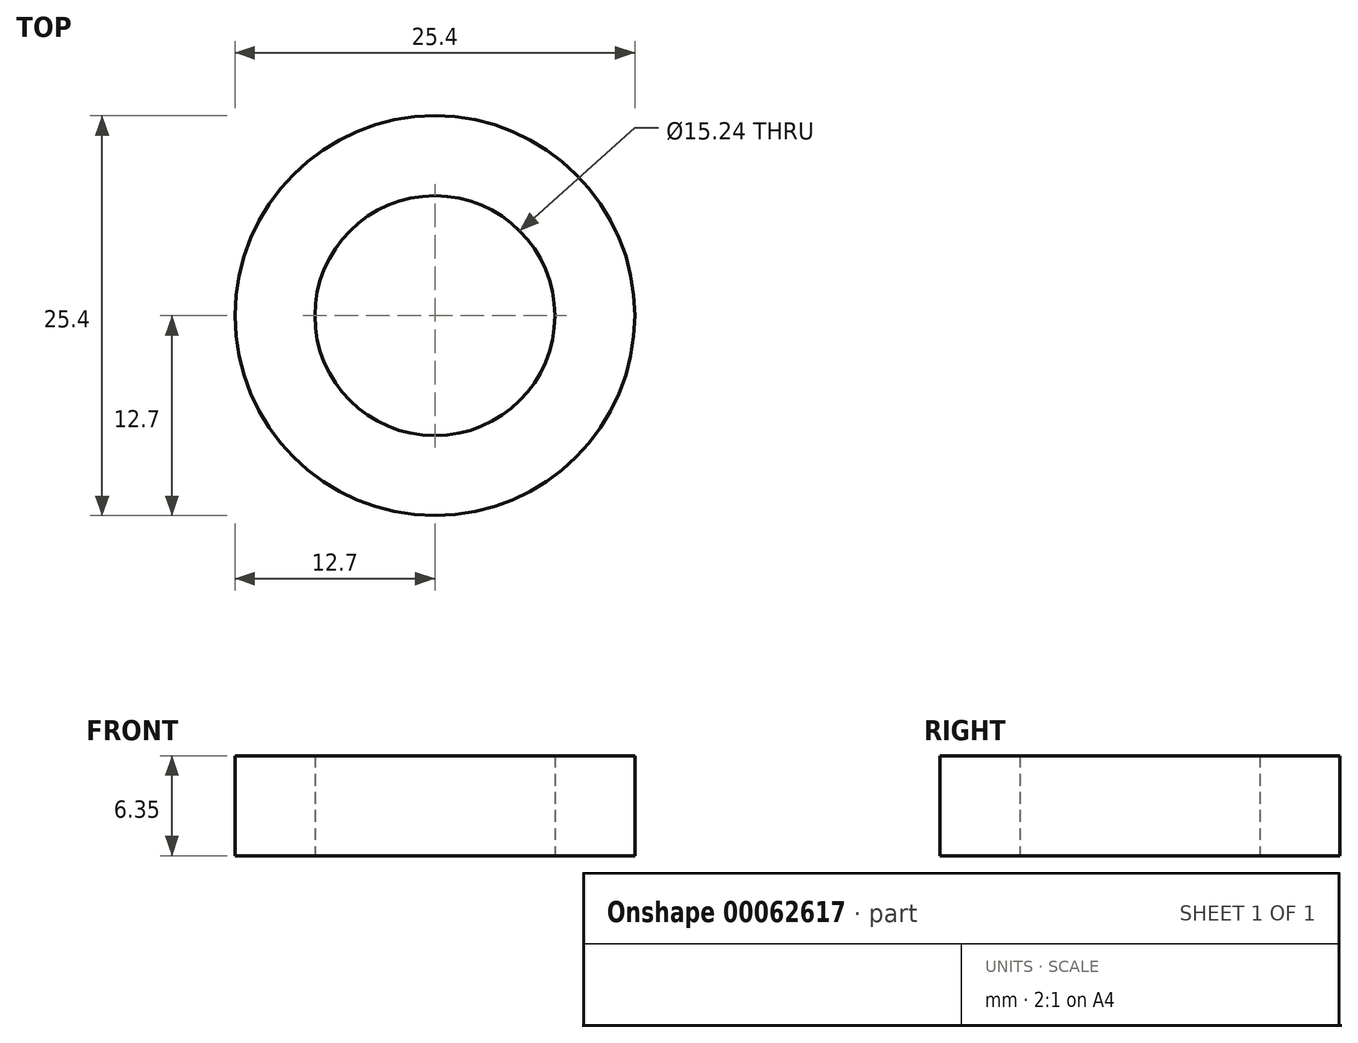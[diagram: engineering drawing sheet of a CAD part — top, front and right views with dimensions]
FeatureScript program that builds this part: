
annotation { "Feature Type Name" : "Feature", "Feature Type Description" : "" }
export const myFeature = defineFeature(function(context is Context, id is Id, definition is map)
    precondition{}
    {
        {
            var Q0;
            Q0=qCreatedBy(makeId("Top.planeOp"),FACE);
            var sketch = newSketch(context, id + "F0", { "sketchPlane" : qUnion([Q0])});
            skCircle(sketch, "E0", {"center": v(0, 0) * mm, "radius": 7.62 * mm});
            skCircle(sketch, "E1", {"center": v(0, 0) * mm, "radius": 12.7 * mm});
            skSolve(sketch);
        }
        {
            var Q0;
            Q0 = qSketchRegion(id + "F0", true);
            extrude(context, id + "F1", {"entities" : qUnion([Q0]), "depth" : 6.35 * mm});
        }
    });
